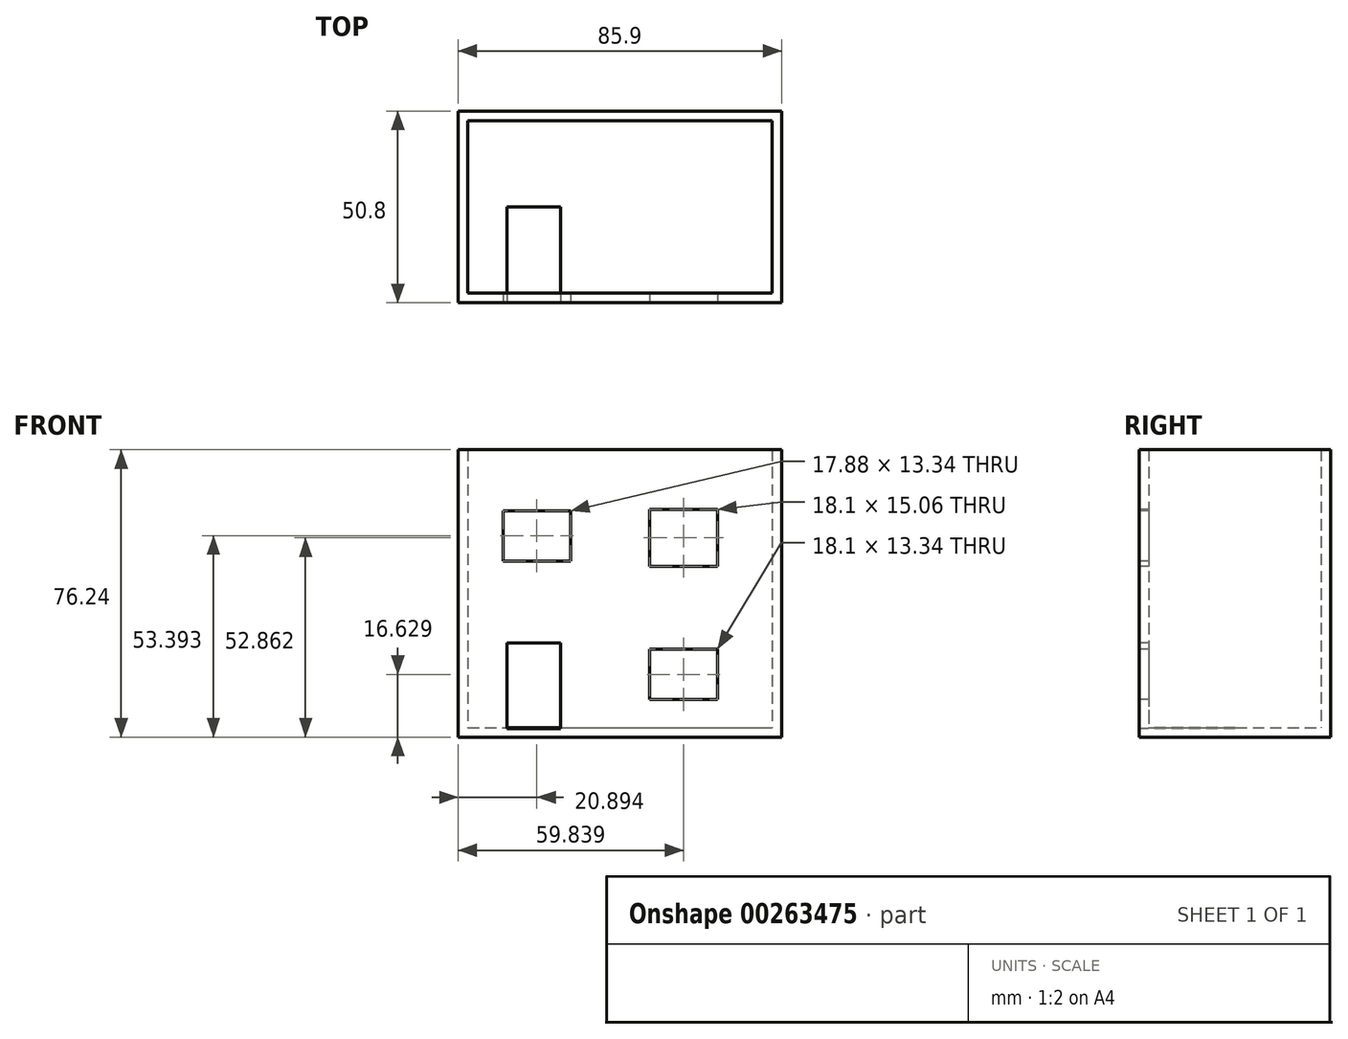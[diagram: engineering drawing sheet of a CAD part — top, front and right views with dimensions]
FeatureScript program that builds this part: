
annotation { "Feature Type Name" : "Feature", "Feature Type Description" : "" }
export const myFeature = defineFeature(function(context is Context, id is Id, definition is map)
    precondition{}
    {
        {
            var Q0;
            Q0=qCreatedBy(makeId("Front.planeOp"),FACE);
            var sketch = newSketch(context, id + "F0", { "sketchPlane" : qUnion([Q0])});
            skLineSegment(sketch, "E0.bottom", {"start": v(-40.95, 0) * mm, "end": v(44.95, 0) * mm});
            skLineSegment(sketch, "E0.top", {"start": v(-40.95, -76.24) * mm, "end": v(44.95, -76.24) * mm});
            skLineSegment(sketch, "E0.left", {"start": v(-40.95, 0) * mm, "end": v(-40.95, -76.24) * mm});
            skLineSegment(sketch, "E0.right", {"start": v(44.95, 0) * mm, "end": v(44.95, -76.24) * mm});
            skSolve(sketch);
        }
        {
            var Q0;
            Q0 = qSketchRegion(id + "F0", true);
            var Q1;
            Q1=sQuery(id+"F0.wireOp",EDGE,"E0.right");
            var Q2;
            Q2=sQuery(id+"F0.wireOp",EDGE,"E0.left");
            var Q3;
            Q3=sQuery(id+"F0.wireOp",EDGE,"E0.bottom");
            var Q4;
            Q4=sQuery(id+"F0.wireOp",EDGE,"E0.top");
            extrude(context, id + "F1", {"entities" : qUnion([Q0]), "surfaceEntities" : qUnion([Q1, Q2, Q3, Q4]), "depth" : 50.8 * mm});
        }
        {
            var Q0;
            Q0=makeQuery(id+"F1.opExtrude","SWEPT_FACE",FACE,{"disambiguationData":[OSD([sQuery(id+"F0.wireOp",EDGE,"E0.bottom")])]});
            shell(context, id + "F2", {"entities" : qUnion([Q0]), "thickness" : 2.54 * mm});
        }
        {
            var Q0;
            Q0=makeQuery(id+"F1.opExtrude","CAP_FACE",FACE,{"disambiguationData":[OSD([sQuery(id+"F0.wireOp",EDGE,"E0.bottom"),sQuery(id+"F0.wireOp",EDGE,"E0.top"),sQuery(id+"F0.wireOp",EDGE,"E0.left"),sQuery(id+"F0.wireOp",EDGE,"E0.right")])],"isStart":false});
            var sketch = newSketch(context, id + "F3", { "sketchPlane" : qUnion([Q0])});
            skLineSegment(sketch, "E1.bottom", {"start": v(-29, -16.18) * mm, "end": v(-11.11, -16.18) * mm});
            skLineSegment(sketch, "E1.top", {"start": v(-29, -29.52) * mm, "end": v(-11.11, -29.52) * mm});
            skLineSegment(sketch, "E1.left", {"start": v(-29, -16.18) * mm, "end": v(-29, -29.52) * mm});
            skLineSegment(sketch, "E1.right", {"start": v(-11.11, -16.18) * mm, "end": v(-11.11, -29.52) * mm});
            skLineSegment(sketch, "E2.bottom", {"start": v(9.84, -15.85) * mm, "end": v(27.94, -15.85) * mm});
            skLineSegment(sketch, "E2.top", {"start": v(9.84, -30.9) * mm, "end": v(27.94, -30.9) * mm});
            skLineSegment(sketch, "E2.left", {"start": v(9.84, -15.85) * mm, "end": v(9.84, -30.9) * mm});
            skLineSegment(sketch, "E2.right", {"start": v(27.94, -15.85) * mm, "end": v(27.94, -30.9) * mm});
            skLineSegment(sketch, "E3.bottom", {"start": v(9.84, -52.94) * mm, "end": v(27.94, -52.94) * mm});
            skLineSegment(sketch, "E3.top", {"start": v(9.84, -66.28) * mm, "end": v(27.94, -66.28) * mm});
            skLineSegment(sketch, "E3.left", {"start": v(9.84, -52.94) * mm, "end": v(9.84, -66.28) * mm});
            skLineSegment(sketch, "E3.right", {"start": v(27.94, -52.94) * mm, "end": v(27.94, -66.28) * mm});
            skLineSegment(sketch, "E4.bottom", {"start": v(-28.06, -51.33) * mm, "end": v(-13.72, -51.33) * mm});
            skLineSegment(sketch, "E4.top", {"start": v(-28.06, -74) * mm, "end": v(-13.72, -74) * mm});
            skLineSegment(sketch, "E4.left", {"start": v(-28.06, -51.33) * mm, "end": v(-28.06, -74) * mm});
            skLineSegment(sketch, "E4.right", {"start": v(-13.72, -51.33) * mm, "end": v(-13.72, -74) * mm});
            skSolve(sketch);
        }
        {
            var Q0;
            Q0 = qSketchRegion(id + "F3", true);
            extrude(context, id + "F4", {"entities" : qUnion([Q0]), "operationType" : NewBodyOperationType.REMOVE, "oppositeDirection" : true, "depth" : 25.4 * mm});
        }
    });
